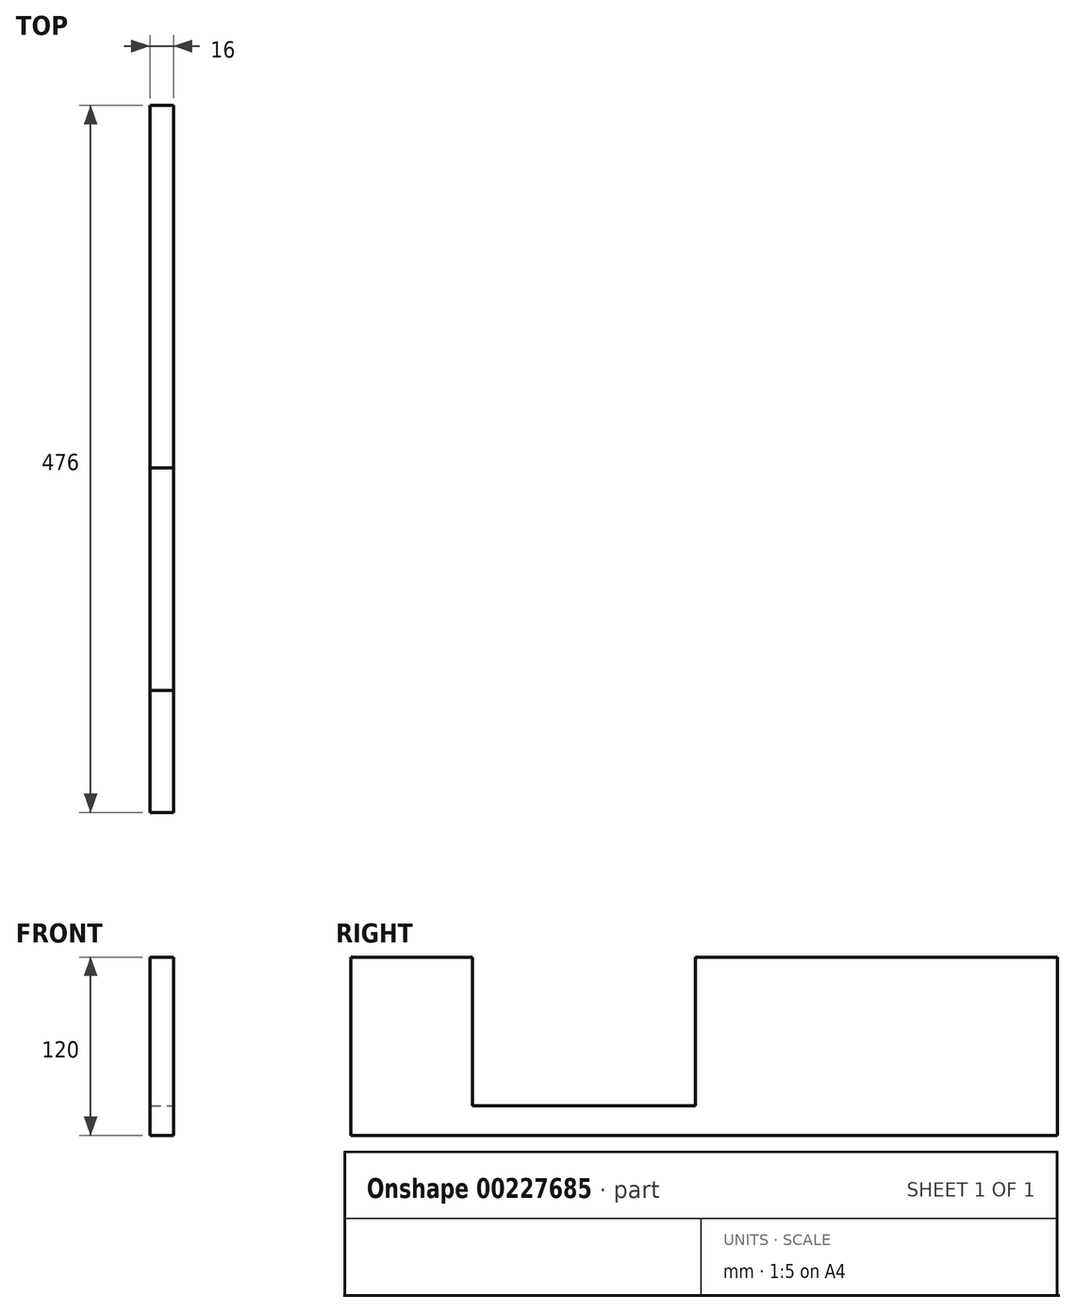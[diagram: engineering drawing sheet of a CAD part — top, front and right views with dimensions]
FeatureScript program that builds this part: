
annotation { "Feature Type Name" : "Feature", "Feature Type Description" : "" }
export const myFeature = defineFeature(function(context is Context, id is Id, definition is map)
    precondition{}
    {
        {
            var Q0;
            Q0=qCreatedBy(makeId("Right.planeOp"),FACE);
            var sketch = newSketch(context, id + "F0", { "sketchPlane" : qUnion([Q0])});
            skLineSegment(sketch, "E0.bottom", {"start": v(238, -60) * mm, "end": v(-238, -60) * mm});
            skLineSegment(sketch, "E0.top", {"start": v(238, 60) * mm, "end": v(-238, 60) * mm});
            skLineSegment(sketch, "E0.left", {"start": v(238, -60) * mm, "end": v(238, 60) * mm});
            skLineSegment(sketch, "E0.right", {"start": v(-238, -60) * mm, "end": v(-238, 60) * mm});
            skPoint(sketch, "E0.middle", {"position": v(0, 0) * mm});
            skSolve(sketch);
        }
        {
            var Q0;
            Q0=qSketchRegion(id+"F0",true);
            extrude(context, id + "F1", {"entities" : qUnion([Q0]), "depth" : 16 * mm, "symmetric" : true});
        }
        {
            var Q0;
            Q0=makeQuery(id+"F1.opExtrude","CAP_FACE",FACE,{"disambiguationData":[OSD([sQuery(id+"F0.wireOp",EDGE,"E0.bottom"),sQuery(id+"F0.wireOp",EDGE,"E0.top"),sQuery(id+"F0.wireOp",EDGE,"E0.left"),sQuery(id+"F0.wireOp",EDGE,"E0.right")])],"isStart":false});
            var sketch = newSketch(context, id + "F2", { "sketchPlane" : qUnion([Q0])});
            skLineSegment(sketch, "E1.bottom", {"start": v(-156, -40) * mm, "end": v(-6, -40) * mm});
            skLineSegment(sketch, "E1.top", {"start": v(-156, 60) * mm, "end": v(-6, 60) * mm});
            skLineSegment(sketch, "E1.left", {"start": v(-156, -40) * mm, "end": v(-156, 60) * mm});
            skLineSegment(sketch, "E1.right", {"start": v(-6, -40) * mm, "end": v(-6, 60) * mm});
            skSolve(sketch);
        }
        {
            var Q0;
            Q0 = qSketchRegion(id + "F2", true);
            extrude(context, id + "F3", {"entities" : qUnion([Q0]), "operationType" : NewBodyOperationType.REMOVE, "endBound" : BoundingType.THROUGH_ALL, "oppositeDirection" : true, "depth" : 25 * mm});
        }
    });
